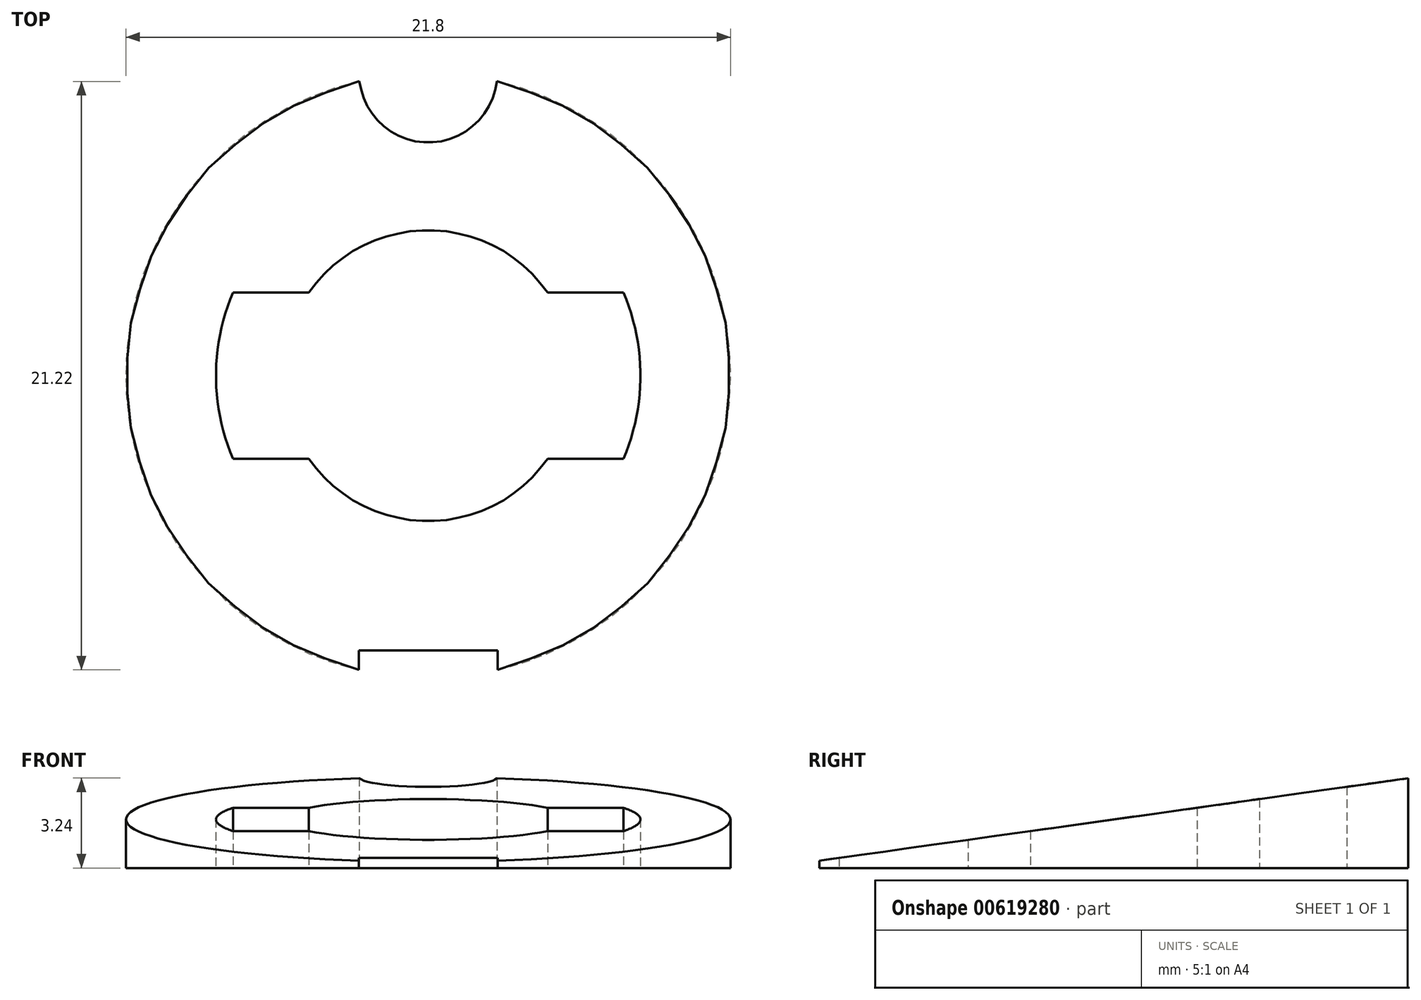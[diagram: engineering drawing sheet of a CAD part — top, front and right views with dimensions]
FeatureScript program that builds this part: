
annotation { "Feature Type Name" : "Feature", "Feature Type Description" : "" }
export const myFeature = defineFeature(function(context is Context, id is Id, definition is map)
    precondition{}
    {
        {
            var Q0;
            Q0=qCreatedBy(makeId("Top.planeOp"),FACE);
            var sketch = newSketch(context, id + "F0", { "sketchPlane" : qUnion([Q0])});
            skArc(sketch, "E0", {"start": v(2.5, -10.6) * mm, "mid": v(0, 10.9) * mm, "end": v(-2.5, -10.6) * mm});
            skArc(sketch, "E1", {"start": v(-7.04, 3) * mm, "mid": v(-7.65, 0) * mm, "end": v(-7.04, -3) * mm});
            skLineSegment(sketch, "E2", {"start": v(0, 10.9) * mm, "end": v(0, 3) * mm, "construction": true});
            skLineSegment(sketch, "E3", {"start": v(4.3, 3) * mm, "end": v(7.04, 3) * mm});
            skLineSegment(sketch, "E4", {"start": v(7.04, 3) * mm, "end": v(4.3, 3) * mm});
            skLineSegment(sketch, "E5", {"start": v(0, 0) * mm, "end": v(0, -9.9) * mm, "construction": true});
            skLineSegment(sketch, "E6", {"start": v(0, -9.9) * mm, "end": v(2.5, -9.9) * mm});
            skLineSegment(sketch, "E7", {"start": v(2.5, -9.9) * mm, "end": v(2.5, -10.6) * mm});
            skLineSegment(sketch, "E8.MirrorCS", {"start": v(0, -9.9) * mm, "end": v(-2.5, -9.9) * mm});
            skLineSegment(sketch, "E9.MirrorCS", {"start": v(-2.5, -9.9) * mm, "end": v(-2.5, -10.6) * mm});
            skLineSegment(sketch, "E10", {"start": v(-7.04, -3) * mm, "end": v(-4.3, -3) * mm});
            skArc(sketch, "E11.trimOffspring", {"start": v(7.04, -3) * mm, "mid": v(7.65, 0) * mm, "end": v(7.04, 3) * mm});
            skArc(sketch, "E12", {"start": v(-4.3, -3) * mm, "mid": v(0, -5.25) * mm, "end": v(4.3, -3) * mm});
            skLineSegment(sketch, "E13.trimOffspring", {"start": v(-4.3, 3) * mm, "end": v(-7.04, 3) * mm});
            skLineSegment(sketch, "E14.trimOffspring", {"start": v(4.3, -3) * mm, "end": v(7.04, -3) * mm});
            skArc(sketch, "E15.trimOffspring", {"start": v(4.3, 3) * mm, "mid": v(0, 5.25) * mm, "end": v(-4.3, 3) * mm});
            skSolve(sketch);
        }
        {
            var Q0;
            Q0=makeQuery(id+"F0.imprint","IMPRINT",FACE,{"disambiguationData":[TD([[makeQuery(id+"F0.imprint","IMPRINT",EDGE,{"derivedFrom":sQuery(id+"F0.wireOp",EDGE,"E0")}),1.0]])]});
            extrude(context, id + "F1", {"entities" : qUnion([Q0]), "depth" : 3.5 * mm, "offsetDistance" : 25 * mm});
        }
        {
            var Q0;
            Q0=qCreatedBy(makeId("Right.planeOp"),FACE);
            var sketch = newSketch(context, id + "F2", { "sketchPlane" : qUnion([Q0])});
            skLineSegment(sketch, "E16", {"start": v(0, 0) * mm, "end": v(0, 3) * mm, "construction": true});
            skLineSegment(sketch, "E17", {"start": v(0, 3) * mm, "end": v(12.5, 2.98) * mm, "construction": true});
            skLineSegment(sketch, "E18", {"start": v(0, 0) * mm, "end": v(-12.5, 0) * mm, "construction": true});
            skLineSegment(sketch, "E19", {"start": v(12.5, 3.5) * mm, "end": v(-12.5, 0) * mm});
            skLineSegment(sketch, "E20", {"start": v(-12.5, 0) * mm, "end": v(-12.5, 3.5) * mm});
            skLineSegment(sketch, "E21", {"start": v(-12.5, 3.5) * mm, "end": v(12.5, 3.5) * mm});
            skSolve(sketch);
        }
        {
            var Q0;
            Q0 = qSketchRegion(id + "F2", true);
            extrude(context, id + "F3", {"entities" : qUnion([Q0]), "operationType" : NewBodyOperationType.REMOVE, "depth" : (25 / 2) * mm, "offsetDistance" : 25 * mm, "hasSecondDirection" : true, "secondDirectionOppositeDirection" : true, "secondDirectionDepth" : (25 / 2) * mm});
        }
        {
            var Q0;
            Q0=qCreatedBy(makeId("Top.planeOp"),FACE);
            var sketch = newSketch(context, id + "F4", { "sketchPlane" : qUnion([Q0])});
            skLineSegment(sketch, "E22", {"start": v(0, 0) * mm, "end": v(0, -6.25) * mm, "construction": true});
            skLineSegment(sketch, "E23", {"start": v(0, -6.25) * mm, "end": v(12, -6.25) * mm});
            skLineSegment(sketch, "E24", {"start": v(12, -6.25) * mm, "end": v(12, -12.5) * mm});
            skLineSegment(sketch, "E25", {"start": v(12, -12.5) * mm, "end": v(-12, -12.5) * mm});
            skLineSegment(sketch, "E26", {"start": v(-12, -12.5) * mm, "end": v(-12, -6.25) * mm});
            skLineSegment(sketch, "E27", {"start": v(-12, -6.25) * mm, "end": v(0, -6.25) * mm});
            skPoint(sketch, "E28.0", {"position": v(0, 10.9) * mm});
            skSolve(sketch);
        }
        {
            var Q0;
            Q0=sQuery(id+"F4.wireOp",VERTEX,"E28.0");
            var Q1;
            Q1=makeQuery(id+"F1.opExtrude","SWEPT_BODY",BODY,{"disambiguationData":[OSD([sQuery(id+"F0.wireOp",EDGE,"E0"),sQuery(id+"F0.wireOp",EDGE,"E1")])]});
            hole(context, id + "F5", {"style" : HoleStyle.SIMPLE, "endStyle" : HoleEndStyle.THROUGH, "oppositeDirection" : true, "holeDiameter" : 5 * mm, "majorDiameter" : 5 * mm, "isTappedThrough" : true, "tappedDepth" : 12 * mm, "tapClearance" : 3, "locations" : qUnion([Q0]), "scope" : qUnion([Q1])});
        }
    });
